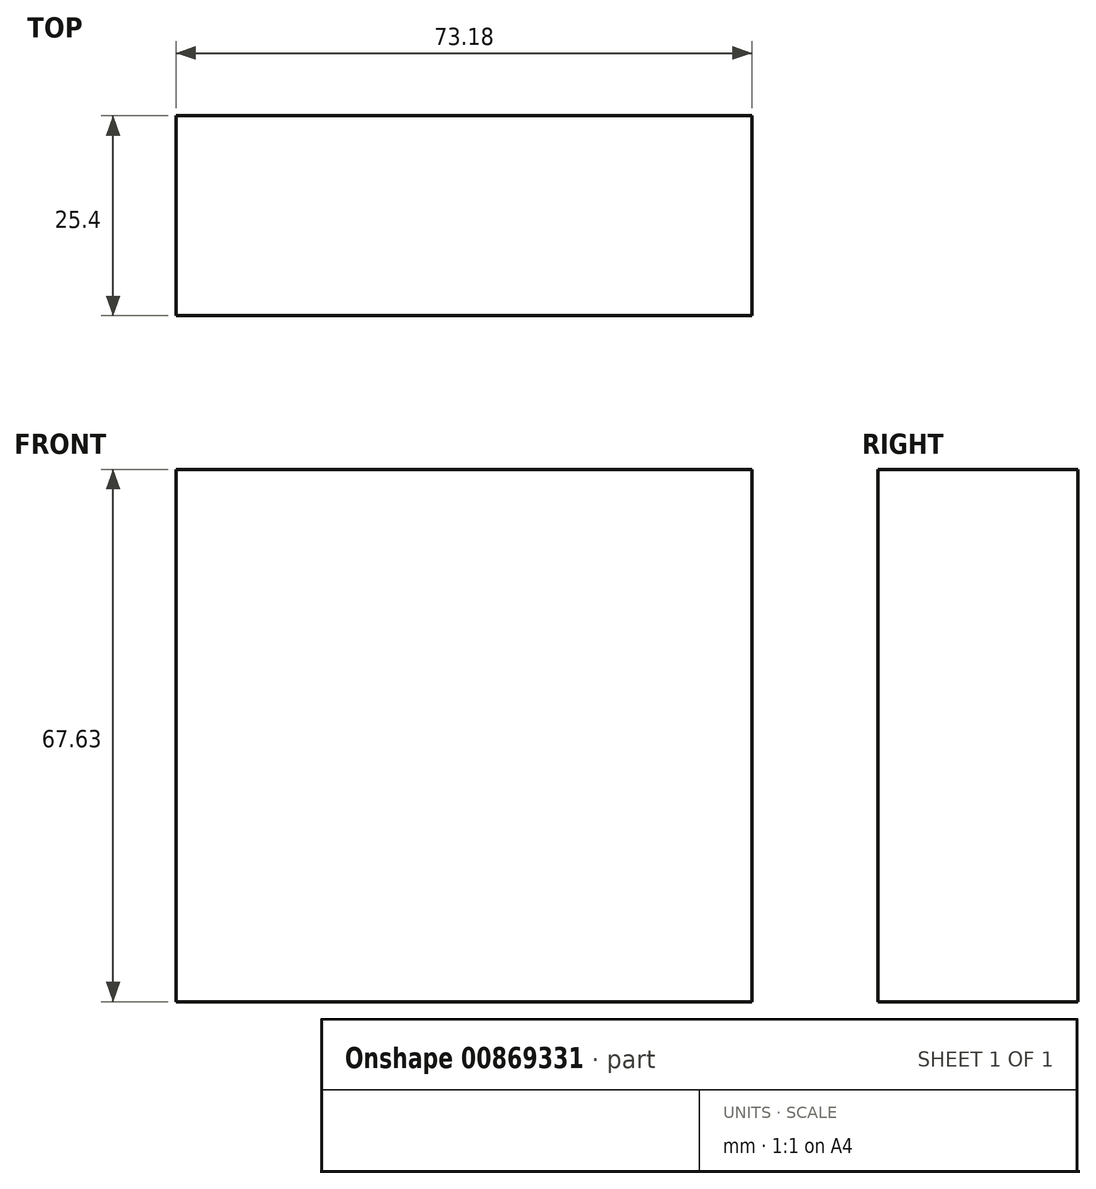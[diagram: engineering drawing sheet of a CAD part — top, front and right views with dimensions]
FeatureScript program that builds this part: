
annotation { "Feature Type Name" : "Feature", "Feature Type Description" : "" }
export const myFeature = defineFeature(function(context is Context, id is Id, definition is map)
    precondition{}
    {
        {
            var Q0;
            Q0=qCreatedBy(makeId("Front.planeOp"),FACE);
            var sketch = newSketch(context, id + "F0", { "sketchPlane" : qUnion([Q0])});
            skLineSegment(sketch, "E0.bottom", {"start": v(-36.22, -25.5) * mm, "end": v(36.96, -25.5) * mm});
            skLineSegment(sketch, "E0.top", {"start": v(-36.22, 42.13) * mm, "end": v(36.96, 42.13) * mm});
            skLineSegment(sketch, "E0.left", {"start": v(-36.22, -25.5) * mm, "end": v(-36.22, 42.13) * mm});
            skLineSegment(sketch, "E0.right", {"start": v(36.96, -25.5) * mm, "end": v(36.96, 42.13) * mm});
            skSolve(sketch);
        }
        {
            var Q0;
            Q0=makeQuery(id+"F0.imprint","IMPRINT",FACE,{"disambiguationData":[TD([[makeQuery(id+"F0.imprint","IMPRINT",EDGE,{"derivedFrom":sQuery(id+"F0.wireOp",EDGE,"E0.bottom")}),1.0]])]});
            extrude(context, id + "F1", {"entities" : qUnion([Q0]), "depth" : 25.4 * mm, "offsetDistance" : 25.4 * mm});
        }
    });
